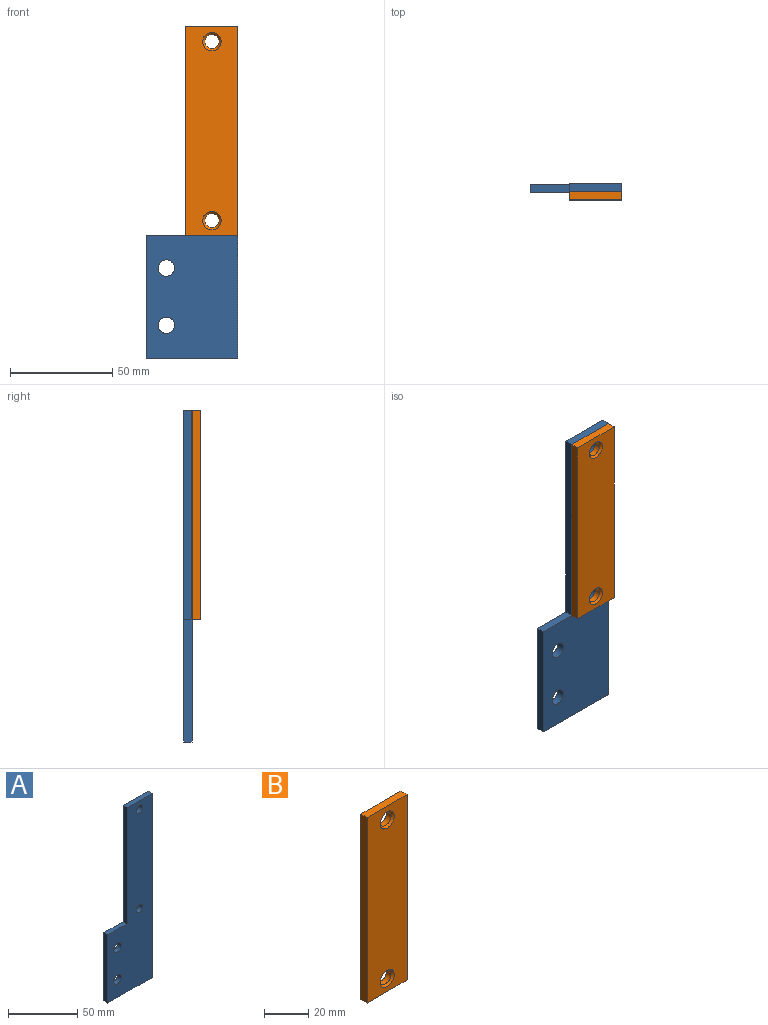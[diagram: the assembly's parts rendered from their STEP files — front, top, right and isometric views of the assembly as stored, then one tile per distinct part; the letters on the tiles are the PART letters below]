
ASSEMBLY  parts=2 mates=1
PART A: 12 faces, bbox 45x4x162.4 mm
  f0: plane 102.4x4mm, normal (-1,0,0), area 409.6mm2, adj f1,f7,f10,f11
  f1: plane 25.48x4mm, normal (0,0,1), area 101.9mm2, adj f0,f2,f10,f11
  f2: plane 162.4x4mm, normal (1,0,0), area 649.6mm2, adj f1,f3,f10,f11
  f3: plane 45x4mm, normal (0,0,-1), area 180mm2, adj f2,f4,f10,f11
  f4: plane 60x4mm, normal (-1,0,0), area 240mm2, adj f3,f7,f10,f11
  f5: cylinder r=4mm len=8mm, axis (0,-1,0), area 100.5mm2, adj f10,f11
  f6: cylinder r=3.5mm len=7mm, axis (0,-1,0), area 88mm2, adj f10,f11
  f7: plane 19.52x4mm, normal (0,0,1), area 78.1mm2, adj f0,f4,f10,f11
  f8: cylinder r=3.5mm len=7mm, axis (0,-1,0), area 88mm2, adj f10,f11
  f9: cylinder r=4mm len=8mm, axis (0,-1,0), area 100.5mm2, adj f10,f11
  f10: plane 162.4x45mm, normal (0,1,0), area 5131.7mm2, adj f0,f1,f2,f3,f4,f5,f6,f7
  f11: plane 162.4x45mm, normal (0,-1,0), area 5131.7mm2, adj f0,f1,f2,f3,f4,f5,f6,f7
PART B: 10 faces, bbox 25.5x4x102.4 mm
  f0: plane 25.48x4mm, normal (0,0,1), area 101.9mm2, adj f1,f5,f6,f7
  f1: plane 102.4x4mm, normal (-1,0,0), area 409.6mm2, adj f0,f2,f6,f7
  f2: plane 25.48x4mm, normal (0,0,-1), area 101.9mm2, adj f1,f5,f6,f7
  f3: cylinder r=3.5mm len=7mm, axis (0,1,0), area 66mm2, adj f7,f9
  f4: cylinder r=3.5mm len=7mm, axis (0,1,0), area 66mm2, adj f7,f8
  f5: plane 102.4x4mm, normal (1,0,0), area 409.6mm2, adj f0,f2,f6,f7
  f6: plane 102.4x25.48mm, normal (0,-1,0), area 2481.9mm2, adj f0,f1,f2,f5,f8,f9
  f7: plane 102.4x25.48mm, normal (0,1,0), area 2532.2mm2, adj f0,f1,f2,f3,f4,f5
  f8: cone r=3.5mm half-angle=45deg, axis (0,-1,0), area 35.5mm2, adj f4,f6
  f9: cone r=3.5mm half-angle=45deg, axis (0,-1,0), area 35.5mm2, adj f3,f6
PLACE A t=(-15.35,29.66,2.11)mm
PLACE B t=(-15.28,31.72,2.15)mm
MATE fastened B.f3 <-> A.f8  axis (0,1,0) through (-15.28,31.72,45.74)mm
